# Revit family: Thermostat Controller For 2 Outlet Use Switch Type_TOTO_TBV02406
name_source: partatom
category: 衛生器具
revit_build: Autodesk Revit 2018 (Build: 20170223_1515(x64)
units: mm (PartAtom-declared; Revit-internal decimal feet)

## family parameters
OmniClass タイトル = Sanitary, Laundry, and Cleaning Equipment
OmniClass 番号 = 23.45.00.00
パーツ タイプ = 標準
ロード時にボイドで切り取り = いいえ
丸型コネクタ寸法 = 直径を使用
作業面ベース = いいえ
共有 = いいえ
常に垂直 = はい
部屋計算ポイント = いいえ

## types (1)
- Thermostat Controller For 2 Outlet Use Switch Type_TOTO_TBV02406
    Finish = faucet_material
    Height = 135  [stored 0.442913 ft]
    Length = 72.7  [stored 0.238517 ft]
    TOTO AsiaOceania = TBV02406B
    TOTO AsiaOceania URL = http://asia.toto.com
    TOTO China = TBV02406B
    TOTO China URL = http://www.toto.com.cn
    TOTO Europe = TBV02406E3
    TOTO Europe URL = https://gb.toto.com
    TOTO India = TBV02406B
    TOTO India URL = https://in.toto.com
    TOTO Korea = TBV02406B
    TOTO Korea URL = https://kr.toto.com
    TOTO Taiwan = TBV02406B
    TOTO Taiwan URL = https://www.twtoto.com.tw
    TOTO Taiwan URL 02 = https://www.twtoto.com.tw
    TOTO Taiwan URL 03 = https://www.twtoto.com.tw
    TOTO Taiwan URL 04 = https://www.twtoto.com.tw
    TOTO Taiwan URL 05 = https://www.twtoto.com.tw
    TOTO Thailand = TBV02406T
    TOTO Thailand URL = https://th.toto.com
    TOTO USA = TBV02406U
    TOTO USA URL = https://www.totousa.com
    TOTO Vietnam = TBV02406B
    TOTO Vietnam URL = https://vn.toto.com
    TOTO Vietnam URL 02 = https://vn.toto.com
    Width = 135  [stored 0.442913 ft]
    タイプの説明 = Required MINI UNIT(TBN1001B)/埋入盒装本体部(TBN01001B)需另购*TEU:TBN01001E3
    モデル = TBV02406
    製造元 = TOTO Ltd.
    説明 = Thermostat Controller For 2 Outlet Use Switch Type/单柄恒温暗装水嘴面板(开闭切换/按启式)

note: [stored X ft] marks values corroborated as IEEE doubles in the binary element streams (Revit-internal decimal feet)

## geometry (parser evidence)
native form markers: Sweep x2
no freeform markers — native parametric forms only
